# Revit family: 9602-PLR
name_source: partatom
category: Plumbing Fixtures
units: mm (PartAtom-declared; Revit-internal decimal feet)

## family parameters
Cut with Voids When Loaded = No
Host = Face
OmniClass Number = 23.65.70.11.11
OmniClass Title = Fixtures for Liquids
Part Type = Normal
Room Calculation Point = No
Round Connector Dimension = Use Diameter
Shared = No

## types (8) — shared parameters
CW Connection = No
HW Connection = No
Model Number = L2
Vent Connection = No
Waste Connection = No
z GPM GPM = 0.000 GPM
z Has .5 Inch Female Connections = Yes
z Has Rebuild Kit Trim Only = No
z Has Trim = No
zero-valued in all types: Default Elevation, z GPM Number, z Type GPM

## per-type parameters (varying)
| type | Gallons Per Minute | Product Material |
| 1.2 GPM Flow Restrictor, Chrome | 1.200 GPM | Chrome - Symmons - Polished |
| 1.2 GPM Flow Restrictor, Satin Nickel | 1.200 GPM | Nickel - Symmons - Satin |
| 1.5 GPM Flow Restrictor, Satin Nickel | 1.500 GPM | Nickel - Symmons - Satin |
| 1.75 GPM Flow Restrictor, Satin Nickel | 1.750 GPM | Nickel - Symmons - Satin |
| 2.0 GPM Flow Restrictor, Satin Nickel | 2.000 GPM | Nickel - Symmons - Satin |
| 1.5 GPM Flow Restrictor, Chrome | 1.500 GPM | Chrome - Symmons - Polished |
| 1.75 GPM Flow Restrictor, Chrome | 1.750 GPM | Chrome - Symmons - Polished |
| 2.0 GPM Flow Restrictor, Chrome | 2.000 GPM | Chrome - Symmons - Polished |

## geometry (parser evidence)
native form markers: Blend x2, Sweep x11
no freeform markers — native parametric forms only
